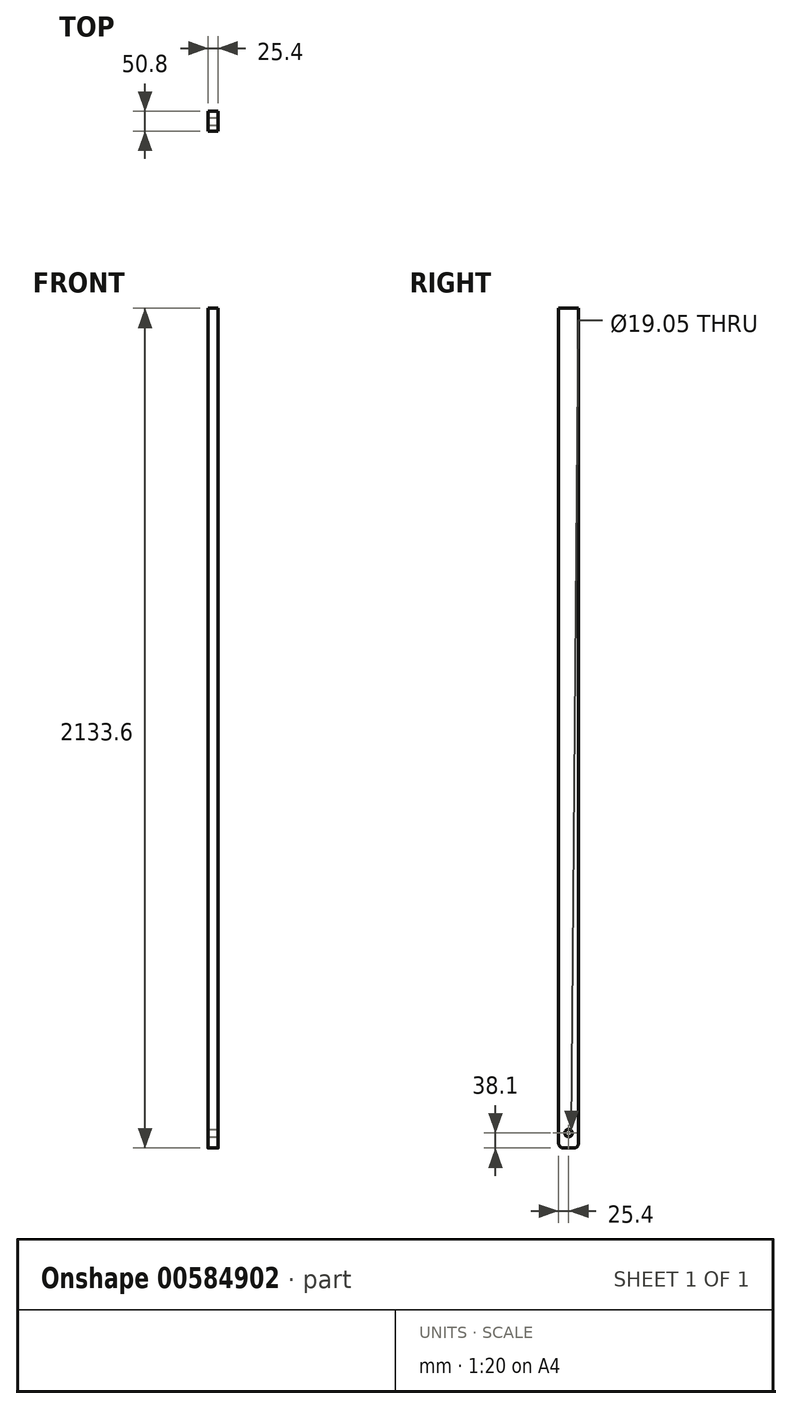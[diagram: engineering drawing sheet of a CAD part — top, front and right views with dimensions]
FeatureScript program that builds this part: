
annotation { "Feature Type Name" : "Feature", "Feature Type Description" : "" }
export const myFeature = defineFeature(function(context is Context, id is Id, definition is map)
    precondition{}
    {
        {
            var Q0;
            Q0=qCreatedBy(makeId("Top.planeOp"),FACE);
            var sketch = newSketch(context, id + "F0", { "sketchPlane" : qUnion([Q0])});
            skLineSegment(sketch, "E0.bottom", {"start": v(12.7, 25.4) * mm, "end": v(-12.7, 25.4) * mm});
            skLineSegment(sketch, "E0.top", {"start": v(12.7, -25.4) * mm, "end": v(-12.7, -25.4) * mm});
            skLineSegment(sketch, "E0.left", {"start": v(12.7, 25.4) * mm, "end": v(12.7, -25.4) * mm});
            skLineSegment(sketch, "E0.right", {"start": v(-12.7, 25.4) * mm, "end": v(-12.7, -25.4) * mm});
            skPoint(sketch, "E0.middle", {"position": v(0, 0) * mm});
            skSolve(sketch);
        }
        {
            var Q0;
            Q0=makeQuery(id+"F0.imprint","IMPRINT",FACE,{"disambiguationData":[TD([[makeQuery(id+"F0.imprint","IMPRINT",EDGE,{"derivedFrom":sQuery(id+"F0.wireOp",EDGE,"E0.bottom")}),1.0]])]});
            extrude(context, id + "F1", {"entities" : qUnion([Q0]), "depth" : 2133.6 * mm, "offsetDistance" : 25.4 * mm});
        }
        {
            var Q0;
            Q0=makeQuery(id+"F1.opExtrude","CAP_EDGE",EDGE,{"disambiguationData":[OSD([sQuery(id+"F0.wireOp",EDGE,"E0.top")])],"isStart":true});
            var Q1;
            Q1=makeQuery(id+"F1.opExtrude","CAP_EDGE",EDGE,{"disambiguationData":[OSD([sQuery(id+"F0.wireOp",EDGE,"E0.bottom")])],"isStart":true});
            fillet(context, id + "F2", {"entities" : qUnion([Q0, Q1]), "radius" : 12.7 * mm, "tangentPropagation" : true, "allowEdgeOverflow" : false});
        }
        {
            var Q0;
            Q0=makeQuery(id+"F1.opExtrude","SWEPT_FACE",FACE,{"disambiguationData":[OSD([sQuery(id+"F0.wireOp",EDGE,"E0.left")])]});
            var sketch = newSketch(context, id + "F3", { "sketchPlane" : qUnion([Q0])});
            skPoint(sketch, "E1", {"position": v(0, 38.1) * mm});
            skSolve(sketch);
        }
        {
            var Q0;
            Q0=sQuery(id+"F3.wireOp",VERTEX,"E1");
            var Q1;
            Q1=makeQuery(id+"F1.opExtrude","SWEPT_BODY",BODY,{"disambiguationData":[OSD([sQuery(id+"F0.wireOp",EDGE,"E0.bottom"),sQuery(id+"F0.wireOp",EDGE,"E0.top"),sQuery(id+"F0.wireOp",EDGE,"E0.left"),sQuery(id+"F0.wireOp",EDGE,"E0.right")])]});
            hole(context, id + "F4", {"style" : HoleStyle.SIMPLE, "endStyle" : HoleEndStyle.THROUGH, "holeDiameter" : 19.05 * mm, "majorDiameter" : 6.35 * mm, "isTappedThrough" : true, "tappedDepth" : 12.7 * mm, "tapClearance" : 3, "locations" : qUnion([Q0]), "scope" : qUnion([Q1])});
        }
    });
